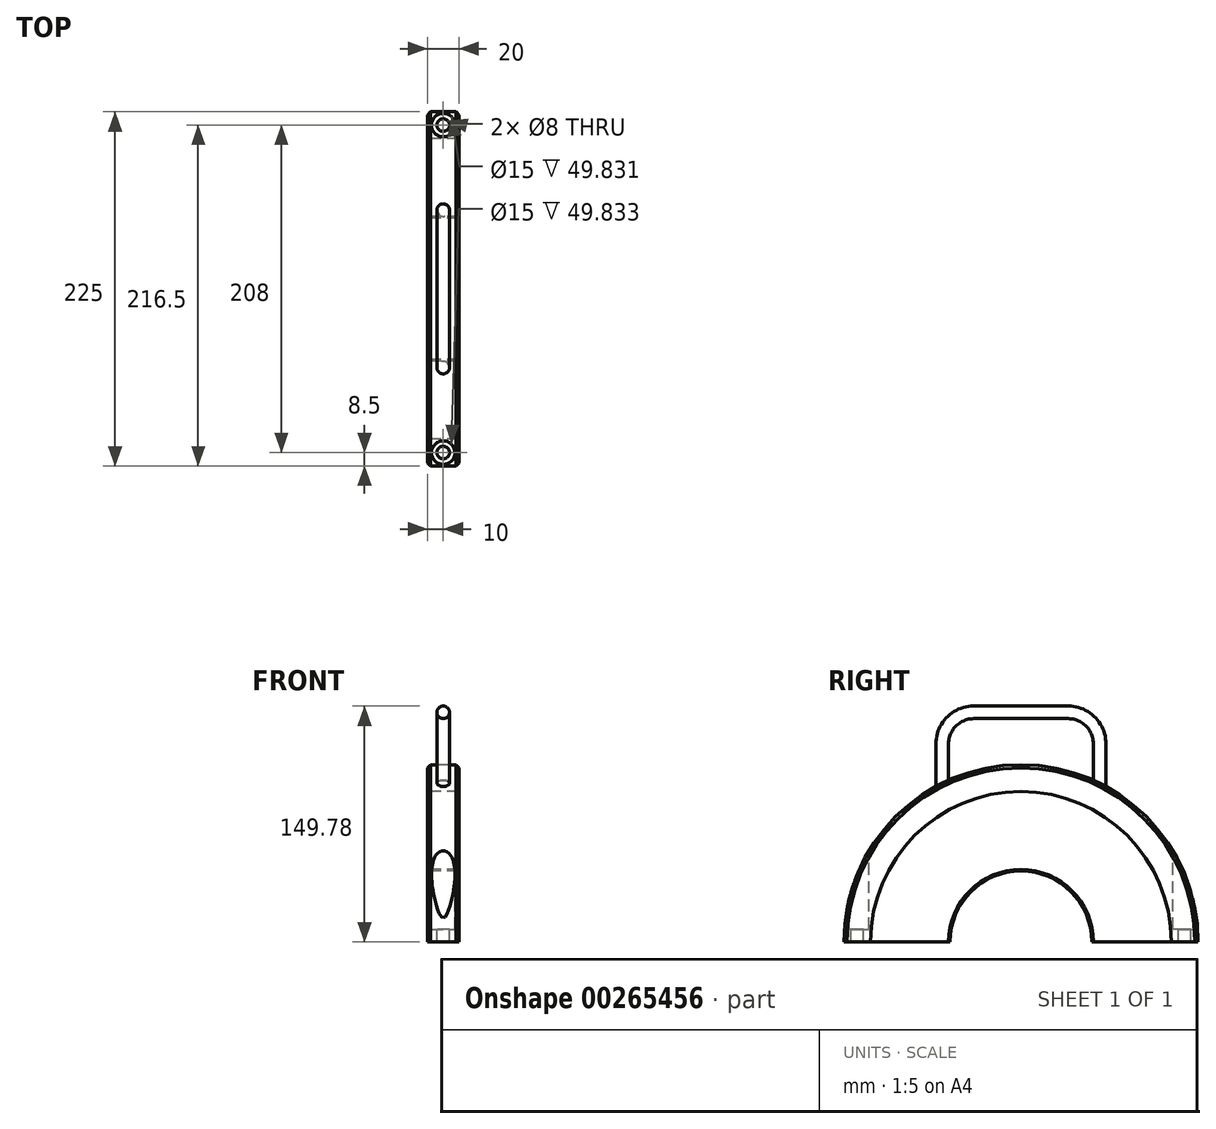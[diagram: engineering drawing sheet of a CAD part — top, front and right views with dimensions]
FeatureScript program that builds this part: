
annotation { "Feature Type Name" : "Feature", "Feature Type Description" : "" }
export const myFeature = defineFeature(function(context is Context, id is Id, definition is map)
    precondition{}
    {
        {
            var Q0;
            Q0=qCreatedBy(makeId("Front.planeOp"),FACE);
            var sketch = newSketch(context, id + "F0", { "sketchPlane" : qUnion([Q0])});
            skLineSegment(sketch, "E0", {"start": v(-48.97, 0) * mm, "end": v(48.97, 0) * mm, "construction": true});
            skLineSegment(sketch, "E1.bottom", {"start": v(-10, 46) * mm, "end": v(10, 46) * mm});
            skLineSegment(sketch, "E1.top", {"start": v(-10, 45) * mm, "end": v(10, 45) * mm});
            skLineSegment(sketch, "E1.left", {"start": v(-10, 46) * mm, "end": v(-10, 45) * mm});
            skLineSegment(sketch, "E1.right", {"start": v(10, 46) * mm, "end": v(10, 45) * mm});
            skLineSegment(sketch, "E2", {"start": v(0, 12.38) * mm, "end": v(0, -12.38) * mm, "construction": true});
            skSolve(sketch);
        }
        {
            var Q0;
            Q0=makeQuery(id+"F0.imprint","IMPRINT",FACE,{"disambiguationData":[TD([[makeQuery(id+"F0.imprint","IMPRINT",EDGE,{"derivedFrom":sQuery(id+"F0.wireOp",EDGE,"E1.bottom")}),-1.0]])]});
            var Q1;
            Q1=sQuery(id+"F0.wireOp",EDGE,"E0");
            revolve(context, id + "F1", {"entities" : qUnion([Q0]), "axis" : qUnion([Q1]), "revolveType" : RevolveType.FULL});
        }
        {
            var Q0;
            Q0=qCreatedBy(makeId("Front.planeOp"),FACE);
            var sketch = newSketch(context, id + "F2", { "sketchPlane" : qUnion([Q0])});
            skLineSegment(sketch, "E3.bottom", {"start": v(-10, 95.5) * mm, "end": v(10, 95.5) * mm});
            skLineSegment(sketch, "E3.top", {"start": v(-10, 46) * mm, "end": v(10, 46) * mm});
            skLineSegment(sketch, "E3.left", {"start": v(-10, 95.5) * mm, "end": v(-10, 46) * mm});
            skLineSegment(sketch, "E3.right", {"start": v(10, 95.5) * mm, "end": v(10, 46) * mm});
            skLineSegment(sketch, "E4", {"start": v(-46.04, 0) * mm, "end": v(46.04, 0) * mm, "construction": true});
            skSolve(sketch);
        }
        {
            var Q0;
            Q0=makeQuery(id+"F2.imprint","IMPRINT",FACE,{"disambiguationData":[TD([[makeQuery(id+"F2.imprint","IMPRINT",EDGE,{"derivedFrom":sQuery(id+"F2.wireOp",EDGE,"E3.bottom")}),-1.0]])]});
            var Q1;
            Q1=sQuery(id+"F2.wireOp",EDGE,"E4");
            revolve(context, id + "F3", {"entities" : qUnion([Q0]), "axis" : qUnion([Q1]), "revolveType" : RevolveType.FULL});
        }
        {
            var Q0;
            Q0=qCreatedBy(makeId("Front.planeOp"),FACE);
            var sketch = newSketch(context, id + "F4", { "sketchPlane" : qUnion([Q0])});
            skLineSegment(sketch, "E5", {"start": v(-40.4, 0) * mm, "end": v(40.4, 0) * mm, "construction": true});
            skLineSegment(sketch, "E6.bottom", {"start": v(-10, 112.5) * mm, "end": v(10, 112.5) * mm});
            skLineSegment(sketch, "E6.top", {"start": v(-10, 95.5) * mm, "end": v(10, 95.5) * mm});
            skLineSegment(sketch, "E6.left", {"start": v(-10, 112.5) * mm, "end": v(-10, 95.5) * mm});
            skLineSegment(sketch, "E6.right", {"start": v(10, 112.5) * mm, "end": v(10, 95.5) * mm});
            skSolve(sketch);
        }
        {
            var Q0;
            Q0=makeQuery(id+"F4.imprint","IMPRINT",FACE,{"disambiguationData":[TD([[makeQuery(id+"F4.imprint","IMPRINT",EDGE,{"derivedFrom":sQuery(id+"F4.wireOp",EDGE,"E6.bottom")}),-1.0]])]});
            var Q1;
            Q1=sQuery(id+"F4.wireOp",EDGE,"E5");
            revolve(context, id + "F5", {"entities" : qUnion([Q0]), "axis" : qUnion([Q1]), "revolveType" : RevolveType.FULL});
        }
        {
            var Q0;
            Q0=qCreatedBy(makeId("Right.planeOp"),FACE);
            var sketch = newSketch(context, id + "F6", { "sketchPlane" : qUnion([Q0])});
            skLineSegment(sketch, "E7", {"start": v(-50, 95.16) * mm, "end": v(-50, 125.78) * mm});
            skLineSegment(sketch, "E8", {"start": v(-30, 145.78) * mm, "end": v(30, 145.78) * mm});
            skLineSegment(sketch, "E9", {"start": v(50, 125.78) * mm, "end": v(50, 95.16) * mm});
            skPoint(sketch, "E10.visualSharp", {"position": v(50, 145.78) * mm});
            skArc(sketch, "E10.filletArc", {"start": v(50, 125.78) * mm, "mid": v(44.14, 139.92) * mm, "end": v(30, 145.78) * mm});
            skPoint(sketch, "E11.visualSharp", {"position": v(-50, 145.78) * mm});
            skArc(sketch, "E11.filletArc", {"start": v(-30, 145.78) * mm, "mid": v(-44.14, 139.92) * mm, "end": v(-50, 125.78) * mm});
            skPoint(sketch, "E12", {"position": v(50, 100.78) * mm});
            skSolve(sketch);
        }
        {
            var Q0;
            Q0=qCreatedBy(makeId("Top.planeOp"),FACE);
            var Q1;
            Q1=sQuery(id+"F6.wireOp",VERTEX,"E7.start");
            cPlane(context, id + "F7", {"entities" : qUnion([Q0, Q1]), "cplaneType" : CPlaneType.PLANE_POINT, "offset" : 25 * mm, "width" : 150 * mm, "height" : 150 * mm});
        }
        {
            var Q0;
            Q0=qCreatedBy(id+"F7.planeOp",FACE);
            var sketch = newSketch(context, id + "F8", { "sketchPlane" : qUnion([Q0])});
            skCircle(sketch, "E13", {"center": v(0, -50) * mm, "radius": 4 * mm});
            skSolve(sketch);
        }
        {
            var Q0;
            Q0=makeQuery(id+"F8.imprint","IMPRINT",FACE,{"disambiguationData":[TD([[makeQuery(id+"F8.imprint","IMPRINT",EDGE,{"derivedFrom":sQuery(id+"F8.wireOp",EDGE,"E13")}),1.0]])]});
            var Q1;
            Q1=sQuery(id+"F6.wireOp",EDGE,"E7");
            var Q2;
            Q2=sQuery(id+"F6.wireOp",EDGE,"E11.filletArc");
            var Q3;
            Q3=sQuery(id+"F6.wireOp",EDGE,"E8");
            var Q4;
            Q4=sQuery(id+"F6.wireOp",EDGE,"E10.filletArc");
            var Q5;
            Q5=sQuery(id+"F6.wireOp",EDGE,"E9");
            sweep(context, id + "F9", {"operationType" : NewBodyOperationType.ADD, "profiles" : qUnion([Q0]), "path" : qUnion([Q1, Q2, Q3, Q4, Q5])});
        }
        {
            var Q0;
            Q0=makeQuery(id+"F5.opRevolve","SWEPT_EDGE",EDGE,{"disambiguationData":[OSD([sQuery(id+"F4.wireOp",EDGE,"E6.bottom"),sQuery(id+"F4.wireOp",EDGE,"E6.right")])]});
            var Q1;
            Q1=makeQuery(id+"F5.opRevolve","SWEPT_EDGE",EDGE,{"disambiguationData":[OSD([sQuery(id+"F4.wireOp",EDGE,"E6.bottom"),sQuery(id+"F4.wireOp",EDGE,"E6.left")])]});
            chamfer(context, id + "F10", {"entities" : qUnion([Q0, Q1]), "width" : 2 * mm, "tangentPropagation" : true});
        }
        {
            var Q0;
            Q0=qCreatedBy(makeId("Front.planeOp"),FACE);
            var sketch = newSketch(context, id + "F11", { "sketchPlane" : qUnion([Q0])});
            skLineSegment(sketch, "E14.bottom", {"start": v(-10, 0) * mm, "end": v(10, 0) * mm});
            skLineSegment(sketch, "E14.top", {"start": v(-10, -115) * mm, "end": v(10, -115) * mm});
            skLineSegment(sketch, "E14.left", {"start": v(-10, 0) * mm, "end": v(-10, -115) * mm});
            skLineSegment(sketch, "E14.right", {"start": v(10, 0) * mm, "end": v(10, -115) * mm});
            skSolve(sketch);
        }
        {
            var Q0;
            Q0 = qSketchRegion(id + "F11", true);
            extrude(context, id + "F12", {"entities" : qUnion([Q0]), "operationType" : NewBodyOperationType.REMOVE, "endBound" : BoundingType.THROUGH_ALL, "depth" : 25 * mm, "hasSecondDirection" : true, "secondDirectionBound" : SecondDirectionBoundingType.THROUGH_ALL, "secondDirectionOppositeDirection" : true, "secondDirectionDepth" : 25 * mm});
        }
        {
            var Q0;
            {var subQ0=sQuery(id+"F4.wireOp",EDGE,"E6.right");var subQ1=sQuery(id+"F4.wireOp",EDGE,"E6.left");var subQ2=sQuery(id+"F4.wireOp",EDGE,"E6.bottom");Q0=makeQuery(id+"F12.boolean.opBoolean","COPY",FACE,{"disambiguationData":[TD([makeQuery(id+"F5.opRevolve","SWEPT_FACE",FACE,{"disambiguationData":[OSD([subQ2])]}),makeQuery(id+"F5.opRevolve","SWEPT_FACE",FACE,{"disambiguationData":[OSD([sQuery(id+"F4.wireOp",EDGE,"E6.top")])]}),makeQuery(id+"F5.opRevolve","SWEPT_FACE",FACE,{"disambiguationData":[OSD([subQ1])]}),makeQuery(id+"F5.opRevolve","SWEPT_FACE",FACE,{"disambiguationData":[OSD([subQ0])]}),makeQuery(id+"F10.opChamfer","BLEND_FACE",FACE,{"disambiguationData":[OSD([subQ2,subQ1])]}),makeQuery(id+"F10.opChamfer","BLEND_FACE",FACE,{"disambiguationData":[OSD([subQ2,subQ0])]})]),OD(0.0)],"derivedFrom":makeQuery(id+"F12.opExtrude","SWEPT_FACE",FACE,{"disambiguationData":[OSD([sQuery(id+"F11.wireOp",EDGE,"E14.bottom")])]})});}
            cPlane(context, id + "F13", {"entities" : qUnion([Q0]), "cplaneType" : CPlaneType.OFFSET, "offset" : 60 * mm, "oppositeDirection" : true, "width" : 150 * mm, "height" : 150 * mm});
        }
        {
            var Q0;
            Q0=qCreatedBy(id+"F13.planeOp",FACE);
            var sketch = newSketch(context, id + "F14", { "sketchPlane" : qUnion([Q0])});
            skCircle(sketch, "E15", {"center": v(0, 104) * mm, "radius": 7.5 * mm});
            skLineSegment(sketch, "E16", {"start": v(0, 112.5) * mm, "end": v(0, 95.5) * mm, "construction": true});
            skPoint(sketch, "E17.MirrorP", {"position": v(0, -104) * mm});
            skCircle(sketch, "E18.MirrorC", {"center": v(0, -104) * mm, "radius": 7.5 * mm});
            skSolve(sketch);
        }
        {
            var Q0;
            Q0 = qSketchRegion(id + "F14", true);
            extrude(context, id + "F15", {"entities" : qUnion([Q0]), "operationType" : NewBodyOperationType.REMOVE, "depth" : 52 * mm});
        }
        {
            var Q0;
            Q0=makeQuery(id+"F15.boolean.opBoolean","COPY",FACE,{"derivedFrom":makeQuery(id+"F15.opExtrude","CAP_FACE",FACE,{"disambiguationData":[OSD([sQuery(id+"F14.wireOp",EDGE,"E15")])],"isStart":false})});
            var sketch = newSketch(context, id + "F16", { "sketchPlane" : qUnion([Q0])});
            skPoint(sketch, "E19.0", {"position": v(0, -104) * mm});
            skPoint(sketch, "E19.1", {"position": v(0, 104) * mm});
            skSolve(sketch);
        }
        {
            var Q0;
            Q0=sQuery(id+"F16.wireOp",VERTEX,"E19.1");
            var Q1;
            Q1=sQuery(id+"F16.wireOp",VERTEX,"E19.0");
            var Q2;
            Q2=makeQuery(id+"F5.opRevolve","SWEPT_BODY",BODY,{"disambiguationData":[OSD([sQuery(id+"F4.wireOp",EDGE,"E6.bottom"),sQuery(id+"F4.wireOp",EDGE,"E6.top"),sQuery(id+"F4.wireOp",EDGE,"E6.left"),sQuery(id+"F4.wireOp",EDGE,"E6.right")])]});
            hole(context, id + "F17", {"style" : HoleStyle.SIMPLE, "endStyle" : HoleEndStyle.THROUGH, "holeDiameter" : 8 * mm, "tappedDepth" : 12 * mm, "tapClearance" : 3, "locations" : qUnion([Q0, Q1]), "scope" : qUnion([Q2])});
        }
    });
